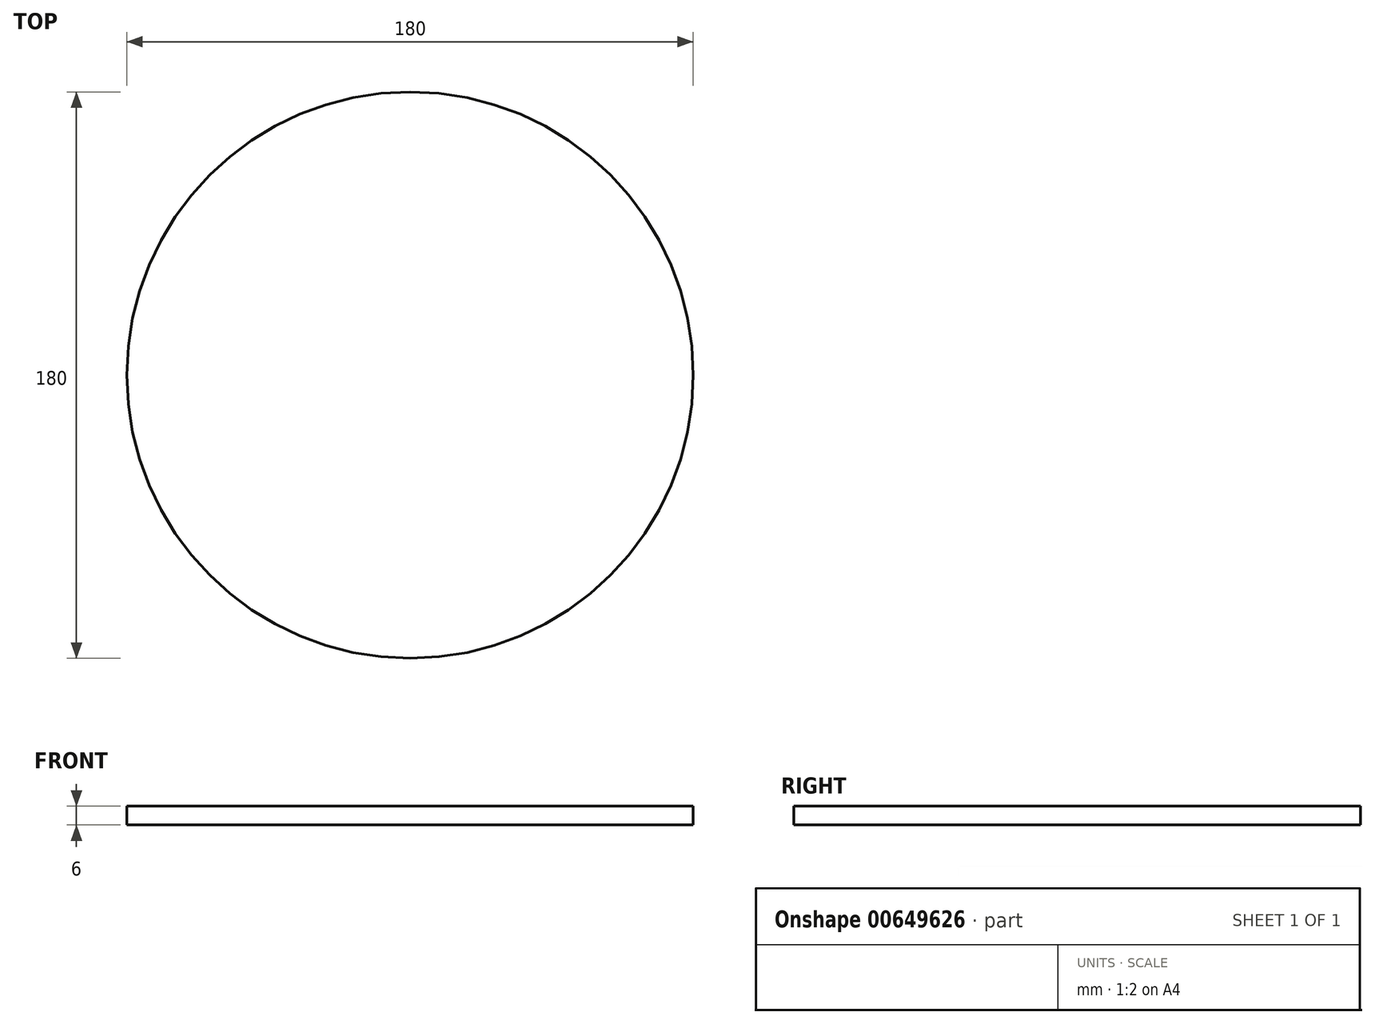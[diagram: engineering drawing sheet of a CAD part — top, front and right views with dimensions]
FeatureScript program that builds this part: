
annotation { "Feature Type Name" : "Feature", "Feature Type Description" : "" }
export const myFeature = defineFeature(function(context is Context, id is Id, definition is map)
    precondition{}
    {
        {
            var Q0;
            Q0=qCreatedBy(makeId("Top.planeOp"),FACE);
            var sketch = newSketch(context, id + "F0", { "sketchPlane" : qUnion([Q0])});
            skCircle(sketch, "E0", {"center": v(0, 0) * mm, "radius": 90 * mm});
            skSolve(sketch);
        }
        {
            var Q0;
            Q0=makeQuery(id+"F0.imprint","IMPRINT",FACE,{"disambiguationData":[TD([[makeQuery(id+"F0.imprint","IMPRINT",EDGE,{"derivedFrom":sQuery(id+"F0.wireOp",EDGE,"E0")}),1.0]])]});
            extrude(context, id + "F1", {"entities" : qUnion([Q0]), "depth" : 6 * mm, "offsetDistance" : 25 * mm});
        }
    });
